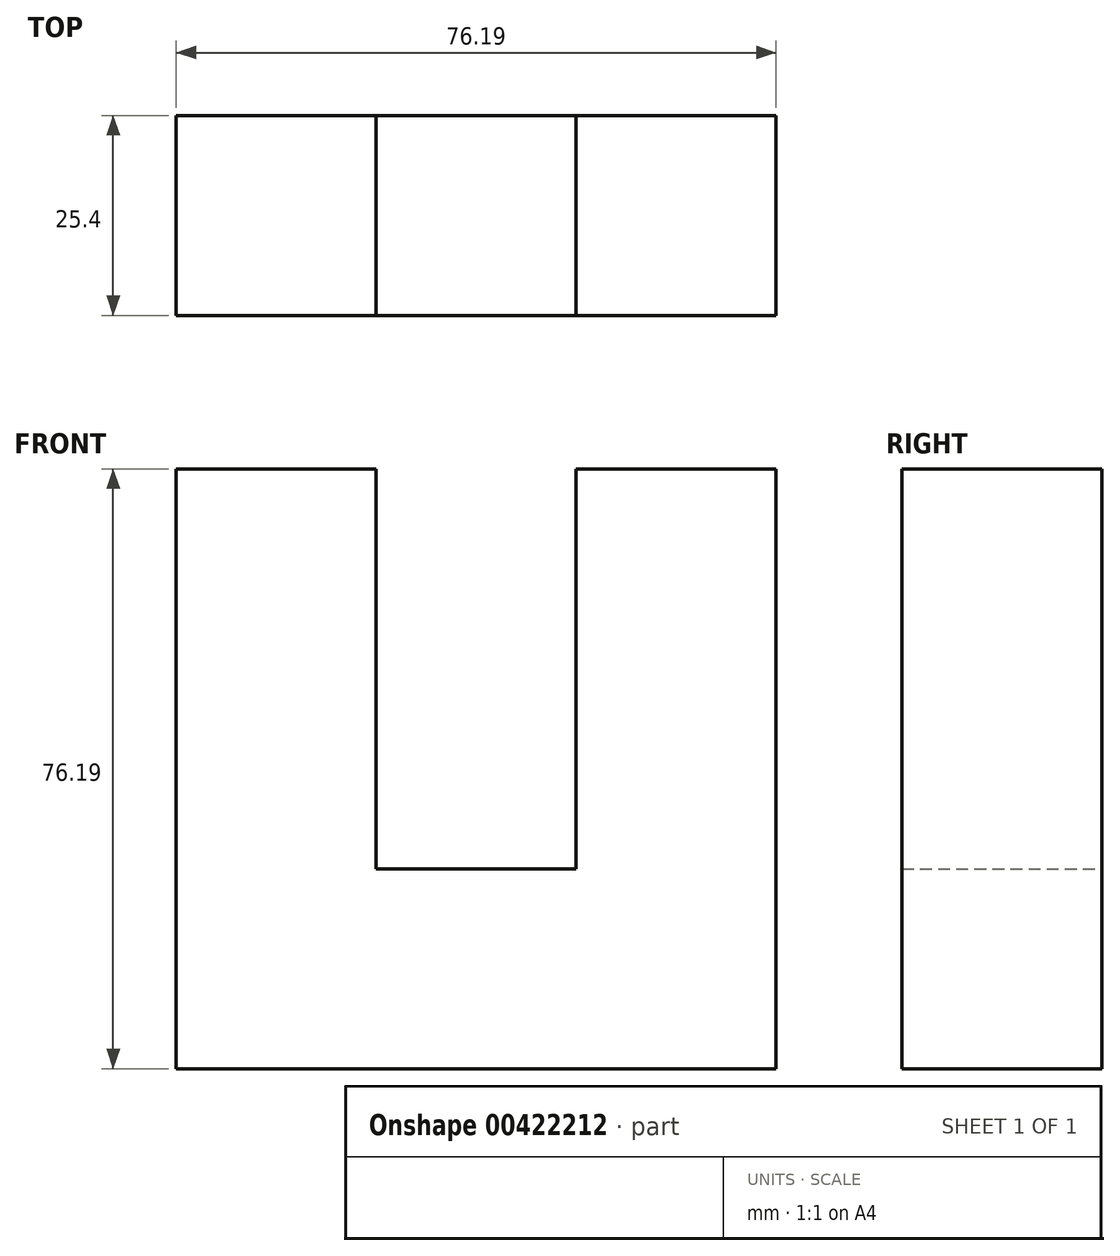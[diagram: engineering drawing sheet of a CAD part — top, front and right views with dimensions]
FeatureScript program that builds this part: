
annotation { "Feature Type Name" : "Feature", "Feature Type Description" : "" }
export const myFeature = defineFeature(function(context is Context, id is Id, definition is map)
    precondition{}
    {
        {
            var Q0;
            Q0=qCreatedBy(makeId("Front.planeOp"),FACE);
            var sketch = newSketch(context, id + "F0", { "sketchPlane" : qUnion([Q0])});
            skLineSegment(sketch, "E0", {"start": v(-68.17, 65.69) * mm, "end": v(-68.17, -10.5) * mm});
            skLineSegment(sketch, "E1", {"start": v(-68.17, -10.5) * mm, "end": v(8.02, -10.5) * mm});
            skLineSegment(sketch, "E2", {"start": v(8.02, -10.5) * mm, "end": v(8.02, 65.69) * mm});
            skLineSegment(sketch, "E3", {"start": v(8.02, 65.69) * mm, "end": v(-17.38, 65.69) * mm});
            skLineSegment(sketch, "E4", {"start": v(-17.38, 65.69) * mm, "end": v(-17.38, 14.9) * mm});
            skLineSegment(sketch, "E5", {"start": v(-17.38, 14.9) * mm, "end": v(-42.77, 14.9) * mm});
            skLineSegment(sketch, "E6", {"start": v(-42.77, 14.9) * mm, "end": v(-42.77, 65.69) * mm});
            skLineSegment(sketch, "E7", {"start": v(-42.77, 65.69) * mm, "end": v(-68.17, 65.69) * mm});
            skSolve(sketch);
        }
        {
            var Q0;
            Q0=makeQuery(id+"F0.imprint","IMPRINT",FACE,{"disambiguationData":[TD([[makeQuery(id+"F0.imprint","IMPRINT",EDGE,{"derivedFrom":sQuery(id+"F0.wireOp",EDGE,"E0")}),1.0]])]});
            extrude(context, id + "F1", {"entities" : qUnion([Q0]), "depth" : 25.4 * mm});
        }
    });
